# Revit family: Toilet_Seat-Elongated_Closed_Front-KOHLER-Impro-K-26802
name_source: partatom
category: Specialty Equipment
units: mm (PartAtom-declared; Revit-internal decimal feet)

## family parameters
Cut with Voids When Loaded = No
Host = Face
OmniClass Number = 23.31.19.19.17
OmniClass Title = Water Closet Seats
Part Type = Normal
Room Calculation Point = No
Round Connector Dimension = Use Diameter
Shared = No

## types (6) — shared parameters
ADA Compliant = No
Assembly Code = C1030200
Date Modified = 12/12/2022
Default Elevation = 15"
Description = Readylatch Quite-Close Parabolic Bowl Toilet Seat
Height = 1 3/4"
Length = 18 1/8"
Manufacturer = Kohler Co.
Master Format 2014 = 10 28 00
Master Format 2014 Name = Toilet, Bath, and Laundry Accessories
Material = Plastic
Product Documentation Link = https://www.us.kohler.com
Product Name = Impro
Product Page URL = http://www.us.kohler.com
URL = https://www.us.kohler.com
WaterSense Certified = No
Width = 14 11/16"

## per-type parameters (varying)
| type | Finish | Model | Type |
| 0-White | Kohler-Plastic-0-White | K-26802-0 | 1 |
| 7-Black Black | Kohler-Plastic-7-Black_Black | K-26802-7 | 2 |
| 58-Thunder Grey | Kohler-Plastic-58-Thunder_Grey | K-26802-58 | 3 |
| 95-Ice Grey | Kohler-Plastic-95-Ice_Grey | K-26802-95 | 4 |
| 96-Biscuit | Kohler-Plastic-96-Biscuit | K-26802-96 | 5 |
| NY-Dune | Kohler-Plastic-NY-Dune | K-26802-NY | 6 |

## geometry (parser evidence)
native form markers: Sweep x5
no freeform markers — native parametric forms only
